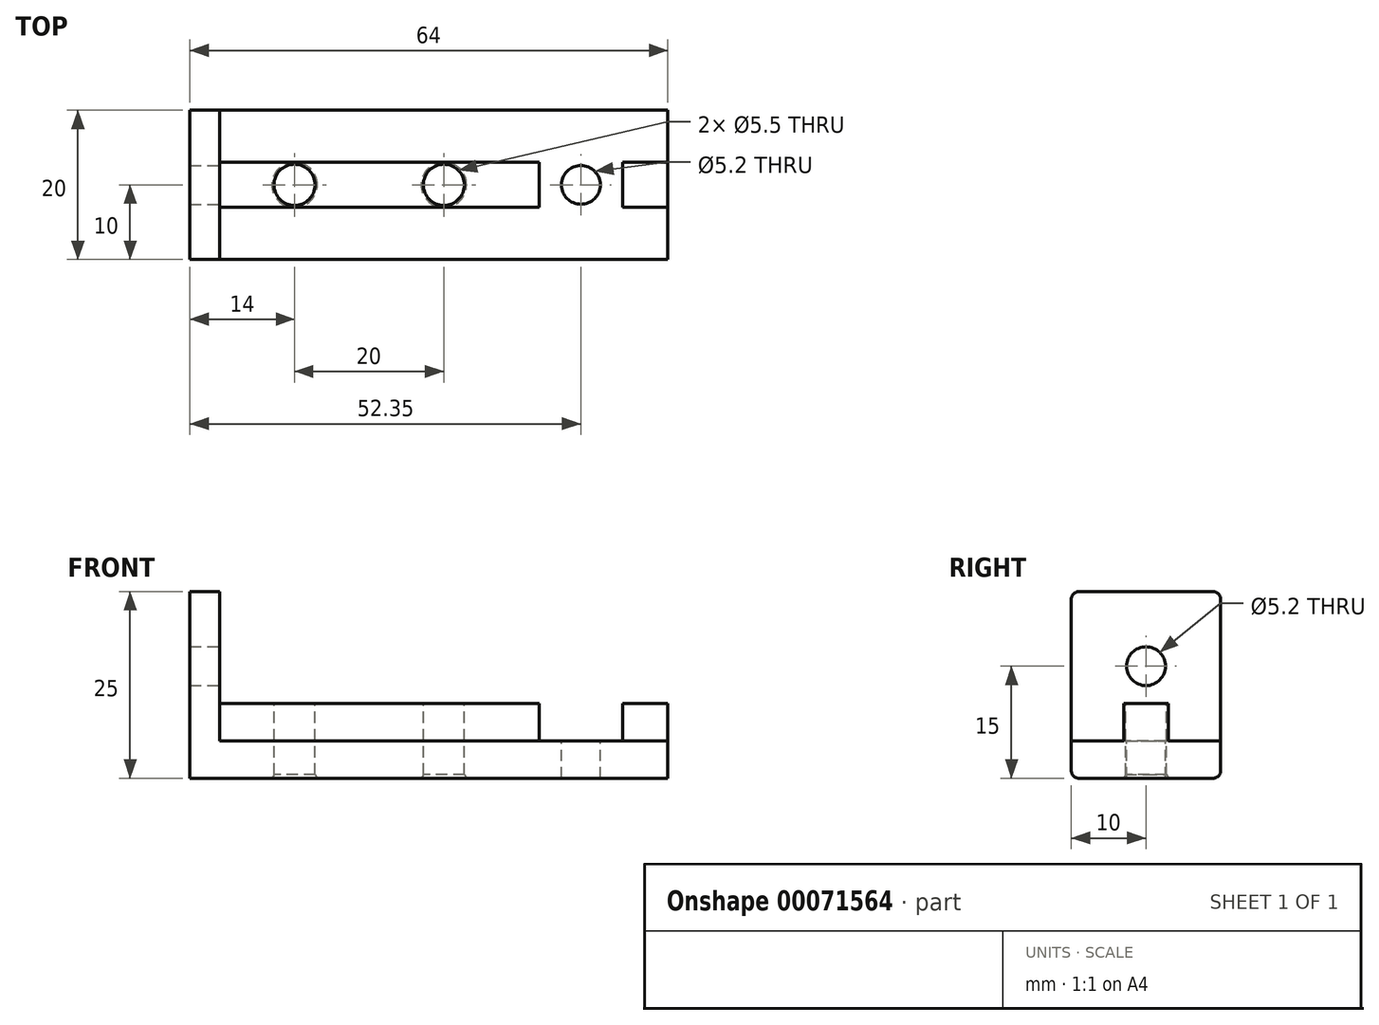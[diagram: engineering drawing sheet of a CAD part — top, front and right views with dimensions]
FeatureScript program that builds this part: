
annotation { "Feature Type Name" : "Feature", "Feature Type Description" : "" }
export const myFeature = defineFeature(function(context is Context, id is Id, definition is map)
    precondition{}
    {
        {
            var Q0;
            Q0=qCreatedBy(makeId("Top.planeOp"),FACE);
            var sketch = newSketch(context, id + "F0", { "sketchPlane" : qUnion([Q0])});
            skLineSegment(sketch, "E0.bottom", {"start": v(0, -10) * mm, "end": v(60, -10) * mm});
            skLineSegment(sketch, "E0.top", {"start": v(0, 10) * mm, "end": v(60, 10) * mm});
            skLineSegment(sketch, "E0.left", {"start": v(0, -10) * mm, "end": v(0, 10) * mm});
            skLineSegment(sketch, "E0.right", {"start": v(60, -10) * mm, "end": v(60, 10) * mm});
            skSolve(sketch);
        }
        {
            var Q0;
            Q0=qSketchRegion(id+"F0",true);
            extrude(context, id + "F1", {"entities" : qUnion([Q0]), "depth" : 5 * mm});
        }
        {
            var Q0;
            Q0=makeQuery(id+"F1.opExtrude","CAP_FACE",FACE,{"disambiguationData":[OSD([sQuery(id+"F0.wireOp",EDGE,"E0.bottom"),sQuery(id+"F0.wireOp",EDGE,"E0.top"),sQuery(id+"F0.wireOp",EDGE,"E0.left"),sQuery(id+"F0.wireOp",EDGE,"E0.right")])],"isStart":false});
            var sketch = newSketch(context, id + "F2", { "sketchPlane" : qUnion([Q0])});
            skLineSegment(sketch, "E1.bottom", {"start": v(0, 3) * mm, "end": v(60, 3) * mm});
            skLineSegment(sketch, "E1.top", {"start": v(0, -3) * mm, "end": v(60, -3) * mm});
            skLineSegment(sketch, "E1.left", {"start": v(0, 3) * mm, "end": v(0, -3) * mm});
            skLineSegment(sketch, "E1.right", {"start": v(60, 3) * mm, "end": v(60, -3) * mm});
            skSolve(sketch);
        }
        {
            var Q0;
            Q0=qSketchRegion(id+"F2",true);
            extrude(context, id + "F3", {"entities" : qUnion([Q0]), "operationType" : NewBodyOperationType.ADD, "depth" : 5 * mm});
        }
        {
            var Q0;
            Q0=makeQuery(id+"F3.opExtrude","CAP_FACE",FACE,{"disambiguationData":[OSD([sQuery(id+"F2.wireOp",EDGE,"E1.bottom"),sQuery(id+"F2.wireOp",EDGE,"E1.top"),sQuery(id+"F2.wireOp",EDGE,"E1.left"),sQuery(id+"F2.wireOp",EDGE,"E1.right")])],"isStart":false});
            var sketch = newSketch(context, id + "F4", { "sketchPlane" : qUnion([Q0])});
            skLineSegment(sketch, "E2", {"start": v(0, 0) * mm, "end": v(10, 0) * mm, "construction": true});
            skLineSegment(sketch, "E3", {"start": v(10, 0) * mm, "end": v(30, 0) * mm, "construction": true});
            skCircle(sketch, "E4", {"center": v(30, 0) * mm, "radius": 2.75 * mm});
            skCircle(sketch, "E5", {"center": v(10, 0) * mm, "radius": 2.75 * mm});
            skSolve(sketch);
        }
        {
            var Q0;
            Q0=qSketchRegion(id+"F4",true);
            extrude(context, id + "F5", {"entities" : qUnion([Q0]), "operationType" : NewBodyOperationType.REMOVE, "oppositeDirection" : true, "depth" : 25 * mm});
        }
        {
            var Q0;
            Q0=makeQuery(id+"F3.opExtrude","CAP_FACE",FACE,{"disambiguationData":[OSD([sQuery(id+"F2.wireOp",EDGE,"E1.bottom"),sQuery(id+"F2.wireOp",EDGE,"E1.top"),sQuery(id+"F2.wireOp",EDGE,"E1.left"),sQuery(id+"F2.wireOp",EDGE,"E1.right")])],"isStart":false});
            var sketch = newSketch(context, id + "F6", { "sketchPlane" : qUnion([Q0])});
            skLineSegment(sketch, "E6.bottom", {"start": v(42.75, 3) * mm, "end": v(53.95, 3) * mm});
            skLineSegment(sketch, "E6.top", {"start": v(42.75, -3) * mm, "end": v(53.95, -3) * mm});
            skLineSegment(sketch, "E6.left", {"start": v(42.75, 3) * mm, "end": v(42.75, -3) * mm});
            skLineSegment(sketch, "E6.right", {"start": v(53.95, 3) * mm, "end": v(53.95, -3) * mm});
            skLineSegment(sketch, "E7", {"start": v(32.75, 0) * mm, "end": v(42.75, 0) * mm, "construction": true});
            skSolve(sketch);
        }
        {
            var Q0;
            Q0=qSketchRegion(id+"F6",true);
            var Q1;
            {var subQ0=sQuery(id+"F0.wireOp",EDGE,"E0.right");var subQ1=sQuery(id+"F0.wireOp",EDGE,"E0.left");var subQ2=sQuery(id+"F0.wireOp",EDGE,"E0.top");Q1=makeQuery(id+"F3.boolean.opBoolean","SPLIT",FACE,{"disambiguationData":[TD([makeQuery(id+"F1.opExtrude","SWEPT_FACE",FACE,{"disambiguationData":[OSD([subQ2])]})])],"derivedFrom":makeQuery(id+"F1.opExtrude","CAP_FACE",FACE,{"disambiguationData":[OSD([sQuery(id+"F0.wireOp",EDGE,"E0.bottom"),subQ2,subQ1,subQ0])],"isStart":false})});}
            extrude(context, id + "F7", {"entities" : qUnion([Q0]), "operationType" : NewBodyOperationType.REMOVE, "endBound" : BoundingType.UP_TO_SURFACE, "oppositeDirection" : true, "endBoundEntityFace" : qUnion([Q1]), "depth" : 25 * mm});
        }
        {
            var Q0;
            {var subQ0=sQuery(id+"F0.wireOp",EDGE,"E0.right");var subQ3=sQuery(id+"F0.wireOp",EDGE,"E0.left");var subQ5=sQuery(id+"F0.wireOp",EDGE,"E0.top");var subQ7=sQuery(id+"F0.wireOp",EDGE,"E0.bottom");var subQ8=makeQuery(id+"F1.opExtrude","CAP_FACE",FACE,{"disambiguationData":[OSD([subQ7,subQ5,subQ3,subQ0])],"isStart":false});Q0=makeQuery(id+"F7.boolean.opBoolean","MERGE",FACE,{"derivedFrom":[makeQuery(id+"F3.boolean.opBoolean","SPLIT",FACE,{"disambiguationData":[TD([makeQuery(id+"F1.opExtrude","SWEPT_FACE",FACE,{"disambiguationData":[OSD([subQ7])]})])],"derivedFrom":subQ8}),makeQuery(id+"F3.boolean.opBoolean","SPLIT",FACE,{"disambiguationData":[TD([makeQuery(id+"F1.opExtrude","SWEPT_FACE",FACE,{"disambiguationData":[OSD([subQ5])]})])],"derivedFrom":subQ8})],"fromTools":[makeQuery(id+"F7.opExtrude","CAP_FACE",FACE,{"disambiguationData":[OSD([sQuery(id+"F6.wireOp",EDGE,"E6.bottom"),sQuery(id+"F6.wireOp",EDGE,"E6.top"),sQuery(id+"F6.wireOp",EDGE,"E6.left"),sQuery(id+"F6.wireOp",EDGE,"E6.right")])],"isStart":false})]});}
            var sketch = newSketch(context, id + "F8", { "sketchPlane" : qUnion([Q0])});
            skLineSegment(sketch, "E8", {"start": v(42.75, 0) * mm, "end": v(53.95, 0) * mm, "construction": true});
            skCircle(sketch, "E9", {"center": v(48.35, 0) * mm, "radius": 2.6 * mm});
            skSolve(sketch);
        }
        {
            var Q0;
            Q0=qSketchRegion(id+"F8",true);
            extrude(context, id + "F9", {"entities" : qUnion([Q0]), "operationType" : NewBodyOperationType.REMOVE, "endBound" : BoundingType.UP_TO_NEXT, "oppositeDirection" : true, "depth" : 25 * mm});
        }
        {
            var Q0;
            Q0=makeQuery(id+"F3.boolean.opBoolean","MERGE",FACE,{"derivedFrom":[makeQuery(id+"F1.opExtrude","SWEPT_FACE",FACE,{"disambiguationData":[OSD([sQuery(id+"F0.wireOp",EDGE,"E0.left")])]}),makeQuery(id+"F3.opExtrude","SWEPT_FACE",FACE,{"disambiguationData":[OSD([sQuery(id+"F2.wireOp",EDGE,"E1.left")])]})]});
            var sketch = newSketch(context, id + "F10", { "sketchPlane" : qUnion([Q0])});
            skLineSegment(sketch, "E10.bottom", {"start": v(-10, 0) * mm, "end": v(10, 0) * mm});
            skLineSegment(sketch, "E10.top", {"start": v(-10, 25) * mm, "end": v(10, 25) * mm});
            skLineSegment(sketch, "E10.left", {"start": v(-10, 0) * mm, "end": v(-10, 25) * mm});
            skLineSegment(sketch, "E10.right", {"start": v(10, 0) * mm, "end": v(10, 25) * mm});
            skCircle(sketch, "E11", {"center": v(0, 15) * mm, "radius": 2.6 * mm});
            skLineSegment(sketch, "E12", {"start": v(0, 15) * mm, "end": v(0, 25) * mm, "construction": true});
            skSolve(sketch);
        }
        {
            var Q0;
            {var subQ11=sQuery(id+"F10.wireOp",EDGE,"E10.top");Q0=makeQuery(id+"F10.imprint","IMPRINT",FACE,{"disambiguationData":[TD([[makeQuery(id+"F10.imprint","IMPRINT",EDGE,{"derivedFrom":subQ11}),-1.0]])]});}
            var Q1;
            {var subQ4=sQuery(id+"F10.wireOp",EDGE,"E10.bottom");Q1=makeQuery(id+"F10.imprint","IMPRINT",FACE,{"disambiguationData":[TD([[makeQuery(id+"F10.imprint","IMPRINT",EDGE,{"derivedFrom":subQ4}),-1.0]])]});}
            extrude(context, id + "F11", {"entities" : qUnion([Q0, Q1]), "operationType" : NewBodyOperationType.ADD, "depth" : 4 * mm});
        }
        {
            var Q0;
            Q0=makeQuery(id+"F11.opExtrude","SWEPT_EDGE",EDGE,{"disambiguationData":[OSD([sQuery(id+"F10.wireOp",EDGE,"E10.top"),sQuery(id+"F10.wireOp",EDGE,"E10.right")])]});
            var Q1;
            Q1=makeQuery(id+"F11.opExtrude","SWEPT_EDGE",EDGE,{"disambiguationData":[OSD([sQuery(id+"F10.wireOp",EDGE,"E10.top"),sQuery(id+"F10.wireOp",EDGE,"E10.left")])]});
            var Q2;
            Q2=makeQuery(id+"F11.boolean.opBoolean","MERGE",EDGE,{"derivedFrom":[makeQuery(id+"F1.opExtrude","CAP_EDGE",EDGE,{"disambiguationData":[OSD([sQuery(id+"F0.wireOp",EDGE,"E0.bottom")])],"isStart":true}),makeQuery(id+"F11.opExtrude","SWEPT_EDGE",EDGE,{"disambiguationData":[OSD([sQuery(id+"F10.wireOp",EDGE,"E10.bottom"),sQuery(id+"F10.wireOp",EDGE,"E10.right")])]})]});
            var Q3;
            Q3=makeQuery(id+"F11.boolean.opBoolean","MERGE",EDGE,{"derivedFrom":[makeQuery(id+"F1.opExtrude","CAP_EDGE",EDGE,{"disambiguationData":[OSD([sQuery(id+"F0.wireOp",EDGE,"E0.top")])],"isStart":true}),makeQuery(id+"F11.opExtrude","SWEPT_EDGE",EDGE,{"disambiguationData":[OSD([sQuery(id+"F10.wireOp",EDGE,"E10.bottom"),sQuery(id+"F10.wireOp",EDGE,"E10.left")])]})]});
            fillet(context, id + "F12", {"entities" : qUnion([Q0, Q1, Q2, Q3]), "radius" : 1 * mm, "tangentPropagation" : true, "allowEdgeOverflow" : false});
        }
        {
            var Q0;
            Q0=makeQuery(id+"F5.boolean.opBoolean","INTERSECT",EDGE,{"derivedFrom":[makeQuery(id+"F1.opExtrude","CAP_FACE",FACE,{"disambiguationData":[OSD([sQuery(id+"F0.wireOp",EDGE,"E0.bottom"),sQuery(id+"F0.wireOp",EDGE,"E0.top"),sQuery(id+"F0.wireOp",EDGE,"E0.left"),sQuery(id+"F0.wireOp",EDGE,"E0.right")])],"isStart":true}),makeQuery(id+"F5.opExtrude","SWEPT_FACE",FACE,{"disambiguationData":[OSD([sQuery(id+"F4.wireOp",EDGE,"E5")])]})]});
            var Q1;
            Q1=makeQuery(id+"F5.boolean.opBoolean","INTERSECT",EDGE,{"derivedFrom":[makeQuery(id+"F1.opExtrude","CAP_FACE",FACE,{"disambiguationData":[OSD([sQuery(id+"F0.wireOp",EDGE,"E0.bottom"),sQuery(id+"F0.wireOp",EDGE,"E0.top"),sQuery(id+"F0.wireOp",EDGE,"E0.left"),sQuery(id+"F0.wireOp",EDGE,"E0.right")])],"isStart":true}),makeQuery(id+"F5.opExtrude","SWEPT_FACE",FACE,{"disambiguationData":[OSD([sQuery(id+"F4.wireOp",EDGE,"E4")])]})]});
            var Q2;
            Q2=makeQuery(id+"F5.boolean.opBoolean","INTERSECT",EDGE,{"derivedFrom":[makeQuery(id+"F1.opExtrude","CAP_FACE",FACE,{"disambiguationData":[OSD([sQuery(id+"F0.wireOp",EDGE,"E0.bottom"),sQuery(id+"F0.wireOp",EDGE,"E0.top"),sQuery(id+"F0.wireOp",EDGE,"E0.left"),sQuery(id+"F0.wireOp",EDGE,"E0.right")])],"isStart":true}),makeQuery(id+"F5.opExtrude","SWEPT_FACE",FACE,{"disambiguationData":[OSD([sQuery(id+"F4.wireOp",EDGE,"09b359c9-9fed-4956-9e02-5c3cf4e6a809")])]})]});
            chamfer(context, id + "F13", {"entities" : qUnion([Q0, Q1, Q2]), "chamferType" : ChamferType.OFFSET_ANGLE, "width" : .5 * mm, "oppositeDirection" : true, "angle" : 30 * degree, "tangentPropagation" : true});
        }
    });
